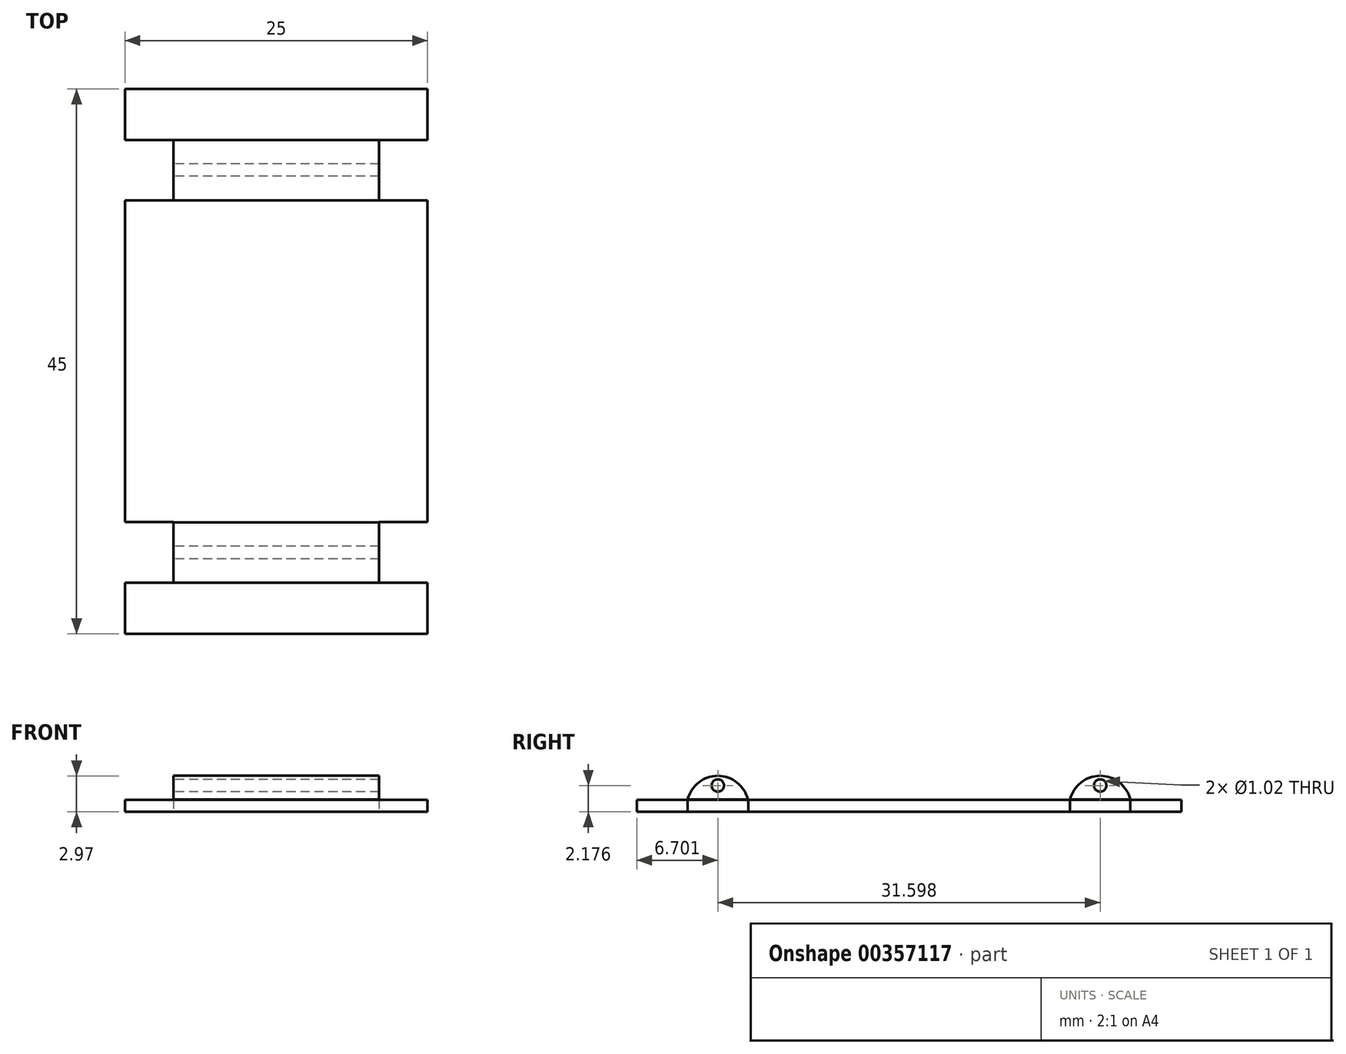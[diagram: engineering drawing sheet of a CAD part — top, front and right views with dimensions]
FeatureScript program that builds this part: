
annotation { "Feature Type Name" : "Feature", "Feature Type Description" : "" }
export const myFeature = defineFeature(function(context is Context, id is Id, definition is map)
    precondition{}
    {
        {
            var Q0;
            Q0=qCreatedBy(makeId("Top.planeOp"),FACE);
            var sketch = newSketch(context, id + "F0", { "sketchPlane" : qUnion([Q0])});
            skLineSegment(sketch, "E0.bottom", {"start": v(-12.5, 22.5) * mm, "end": v(12.5, 22.5) * mm});
            skLineSegment(sketch, "E0.top", {"start": v(-12.5, -22.5) * mm, "end": v(12.5, -22.5) * mm});
            skLineSegment(sketch, "E0.left", {"start": v(-12.5, 22.5) * mm, "end": v(-12.5, 18.28) * mm});
            skLineSegment(sketch, "E0.right", {"start": v(12.5, 22.5) * mm, "end": v(12.5, 18.28) * mm});
            skPoint(sketch, "E0.middle", {"position": v(0, 0) * mm});
            skLineSegment(sketch, "E1.bottom", {"start": v(-8.5, 13.28) * mm, "end": v(-12.5, 13.28) * mm});
            skLineSegment(sketch, "E1.top", {"start": v(-8.5, 18.28) * mm, "end": v(-12.5, 18.28) * mm});
            skLineSegment(sketch, "E1.left", {"start": v(-8.5, 13.28) * mm, "end": v(-8.5, 18.28) * mm});
            skLineSegment(sketch, "E2.MirrorCS", {"start": v(8.5, 13.28) * mm, "end": v(8.5, 18.28) * mm});
            skLineSegment(sketch, "E3.MirrorCS", {"start": v(8.5, 18.28) * mm, "end": v(12.5, 18.28) * mm});
            skLineSegment(sketch, "E4.MirrorCS", {"start": v(8.5, 13.28) * mm, "end": v(12.5, 13.28) * mm});
            skLineSegment(sketch, "E5.MirrorCS", {"start": v(8.5, -13.28) * mm, "end": v(12.5, -13.28) * mm});
            skLineSegment(sketch, "E6.MirrorCS", {"start": v(8.5, -18.28) * mm, "end": v(12.5, -18.28) * mm});
            skLineSegment(sketch, "E7.MirrorCS", {"start": v(8.5, -13.28) * mm, "end": v(8.5, -18.28) * mm});
            skLineSegment(sketch, "E8.MirrorCS", {"start": v(-8.5, -13.28) * mm, "end": v(-12.5, -13.28) * mm});
            skLineSegment(sketch, "E9.MirrorCS", {"start": v(-8.5, -18.28) * mm, "end": v(-12.5, -18.28) * mm});
            skLineSegment(sketch, "E10.MirrorCS", {"start": v(-8.5, -13.28) * mm, "end": v(-8.5, -18.28) * mm});
            skPoint(sketch, "E11.MirrorCS.end.orphan", {"position": v(12.5, 18.28) * mm});
            skPoint(sketch, "E11.MirrorCS.start.orphan", {"position": v(12.5, 13.28) * mm});
            skLineSegment(sketch, "E12.trimOffspring", {"start": v(12.5, -18.28) * mm, "end": v(12.5, -22.5) * mm});
            skPoint(sketch, "E13.MirrorCS.end.orphan", {"position": v(-12.5, -18.28) * mm});
            skPoint(sketch, "E13.MirrorCS.start.orphan", {"position": v(-12.5, -13.28) * mm});
            skLineSegment(sketch, "E14.trimOffspring", {"start": v(-12.5, 13.28) * mm, "end": v(-12.5, -13.28) * mm});
            skLineSegment(sketch, "E15.trimOffspring", {"start": v(12.5, 13.28) * mm, "end": v(12.5, -13.28) * mm});
            skLineSegment(sketch, "E16.trimOffspring", {"start": v(-12.5, -18.28) * mm, "end": v(-12.5, -22.5) * mm});
            skSolve(sketch);
        }
        {
            var Q0;
            Q0 = qSketchRegion(id + "F0", true);
            extrude(context, id + "F1", {"entities" : qUnion([Q0]), "depth" : 1 * mm});
        }
        {
            var Q0;
            Q0=qCreatedBy(makeId("Right.planeOp"),FACE);
            var sketch = newSketch(context, id + "F2", { "sketchPlane" : qUnion([Q0])});
            skArc(sketch, "E17", {"start": v(-13.31, 1.02) * mm, "mid": v(-15.8, 2.97) * mm, "end": v(-18.28, 1.02) * mm});
            skCircle(sketch, "E18", {"center": v(-15.8, 2.18) * mm, "radius": 0.5 * mm});
            skPoint(sketch, "E18.centerSnap0", {"position": v(-15.8, 2.97) * mm});
            skArc(sketch, "E19.MirrorCS", {"start": v(13.31, 1.02) * mm, "mid": v(15.8, 2.97) * mm, "end": v(18.28, 1.02) * mm});
            skCircle(sketch, "E20.MirrorC", {"center": v(15.8, 2.18) * mm, "radius": 0.5 * mm});
            skLineSegment(sketch, "E21", {"start": v(-18.28, 1.02) * mm, "end": v(-13.31, 1.02) * mm});
            skLineSegment(sketch, "E22.MirrorCS", {"start": v(18.28, 1.02) * mm, "end": v(13.31, 1.02) * mm});
            skSolve(sketch);
        }
        {
            var Q0;
            Q0 = qSketchRegion(id + "F2", true);
            extrude(context, id + "F3", {"entities" : qUnion([Q0]), "endBound" : BoundingType.SYMMETRIC, "depth" : 17 * mm});
        }
    });
